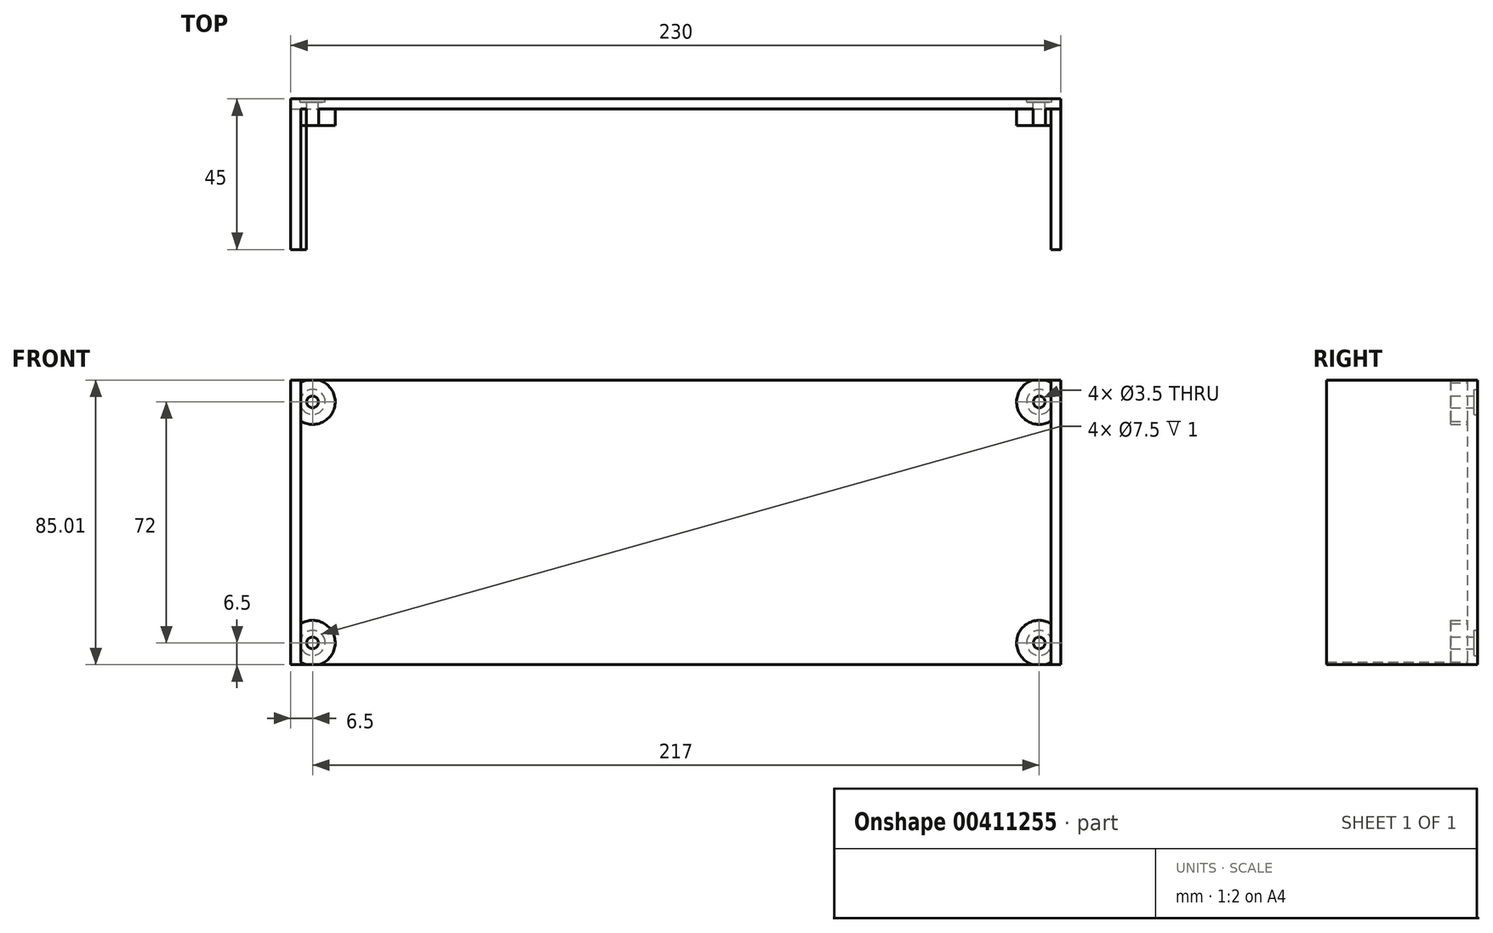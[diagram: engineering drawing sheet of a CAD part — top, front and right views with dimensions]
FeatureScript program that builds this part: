
annotation { "Feature Type Name" : "Feature", "Feature Type Description" : "" }
export const myFeature = defineFeature(function(context is Context, id is Id, definition is map)
    precondition{}
    {
        {
            var Q0;
            Q0=qCreatedBy(makeId("Front.planeOp"),FACE);
            var sketch = newSketch(context, id + "F0", { "sketchPlane" : qUnion([Q0])});
            skLineSegment(sketch, "E0.bottom", {"start": v(-115, 42.5) * mm, "end": v(115, 42.5) * mm});
            skLineSegment(sketch, "E0.top", {"start": v(-115, -42.5) * mm, "end": v(115, -42.5) * mm});
            skLineSegment(sketch, "E0.left", {"start": v(-115, 42.5) * mm, "end": v(-115, -42.5) * mm});
            skLineSegment(sketch, "E0.right", {"start": v(115, 42.5) * mm, "end": v(115, -42.5) * mm});
            skCircle(sketch, "E1", {"center": v(-108.5, 36) * mm, "radius": 1.75 * mm});
            skCircle(sketch, "E2", {"center": v(108.5, 36) * mm, "radius": 1.75 * mm});
            skCircle(sketch, "E3", {"center": v(108.5, -36) * mm, "radius": 1.75 * mm});
            skCircle(sketch, "E4", {"center": v(-108.5, -36) * mm, "radius": 1.75 * mm});
            skSolve(sketch);
        }
        {
            var Q0;
            Q0=makeQuery(id+"F0.imprint","IMPRINT",FACE,{"disambiguationData":[TD([[makeQuery(id+"F0.imprint","IMPRINT",EDGE,{"derivedFrom":sQuery(id+"F0.wireOp",EDGE,"E0.bottom")}),-1.0]])]});
            extrude(context, id + "F1", {"entities" : qUnion([Q0]), "depth" : 3 * mm});
        }
        {
            var Q0;
            Q0=qCreatedBy(makeId("Front.planeOp"),FACE);
            var sketch = newSketch(context, id + "F2", { "sketchPlane" : qUnion([Q0])});
            skCircle(sketch, "E5.0", {"center": v(108.5, 36) * mm, "radius": 3.75 * mm});
            skCircle(sketch, "E6.0", {"center": v(-108.5, 36) * mm, "radius": 3.75 * mm});
            skCircle(sketch, "E7.0", {"center": v(-108.5, -36) * mm, "radius": 3.75 * mm});
            skCircle(sketch, "E8.0", {"center": v(108.5, -36) * mm, "radius": 3.75 * mm});
            skSolve(sketch);
        }
        {
            var Q0;
            Q0 = qSketchRegion(id + "F2", true);
            extrude(context, id + "F3", {"entities" : qUnion([Q0]), "operationType" : NewBodyOperationType.REMOVE, "depth" : 1 * mm});
        }
        {
            var Q0;
            Q0=makeQuery(id+"F1.opExtrude","CAP_FACE",FACE,{"disambiguationData":[OSD([sQuery(id+"F0.wireOp",EDGE,"E0.bottom"),sQuery(id+"F0.wireOp",EDGE,"E0.top"),sQuery(id+"F0.wireOp",EDGE,"E0.left"),sQuery(id+"F0.wireOp",EDGE,"E0.right"),sQuery(id+"F0.wireOp",EDGE,"E1"),sQuery(id+"F0.wireOp",EDGE,"E2"),sQuery(id+"F0.wireOp",EDGE,"E3"),sQuery(id+"F0.wireOp",EDGE,"E4")])],"isStart":false});
            var sketch = newSketch(context, id + "F4", { "sketchPlane" : qUnion([Q0])});
            skCircle(sketch, "E9.0", {"center": v(-108.5, 36) * mm, "radius": 6.75 * mm});
            skCircle(sketch, "E10.0", {"center": v(-108.5, -36) * mm, "radius": 6.75 * mm});
            skCircle(sketch, "E11.0", {"center": v(108.5, 36) * mm, "radius": 6.75 * mm});
            skCircle(sketch, "E12.0", {"center": v(108.5, -36) * mm, "radius": 6.75 * mm});
            skSolve(sketch);
        }
        {
            var Q0;
            Q0=makeQuery(id+"F4.imprint","IMPRINT",FACE,{"disambiguationData":[TD([[makeQuery(id+"F4.imprint","IMPRINT",EDGE,{"derivedFrom":makeQuery(id+"F1.opExtrude","CAP_EDGE",EDGE,{"disambiguationData":[OSD([sQuery(id+"F0.wireOp",EDGE,"E1")])],"isStart":false})}),-1.0]])]});
            var Q1;
            Q1=makeQuery(id+"F4.imprint","IMPRINT",FACE,{"disambiguationData":[TD([[makeQuery(id+"F4.imprint","IMPRINT",EDGE,{"derivedFrom":makeQuery(id+"F1.opExtrude","CAP_EDGE",EDGE,{"disambiguationData":[OSD([sQuery(id+"F0.wireOp",EDGE,"E4")])],"isStart":false})}),-1.0]])]});
            var Q2;
            Q2=makeQuery(id+"F4.imprint","IMPRINT",FACE,{"disambiguationData":[TD([[makeQuery(id+"F4.imprint","IMPRINT",EDGE,{"derivedFrom":makeQuery(id+"F1.opExtrude","CAP_EDGE",EDGE,{"disambiguationData":[OSD([sQuery(id+"F0.wireOp",EDGE,"E2")])],"isStart":false})}),-1.0]])]});
            var Q3;
            Q3=makeQuery(id+"F4.imprint","IMPRINT",FACE,{"disambiguationData":[TD([[makeQuery(id+"F4.imprint","IMPRINT",EDGE,{"derivedFrom":makeQuery(id+"F1.opExtrude","CAP_EDGE",EDGE,{"disambiguationData":[OSD([sQuery(id+"F0.wireOp",EDGE,"E3")])],"isStart":false})}),-1.0]])]});
            extrude(context, id + "F5", {"entities" : qUnion([Q0, Q1, Q2, Q3]), "operationType" : NewBodyOperationType.ADD, "depth" : 5 * mm});
        }
        {
            var Q0;
            Q0=makeQuery(id+"F0.imprint","IMPRINT",FACE,{"disambiguationData":[TD([[makeQuery(id+"F0.imprint","IMPRINT",EDGE,{"derivedFrom":sQuery(id+"F0.wireOp",EDGE,"E4")}),1.0]])]});
            var Q1;
            Q1=makeQuery(id+"F0.imprint","IMPRINT",FACE,{"disambiguationData":[TD([[makeQuery(id+"F0.imprint","IMPRINT",EDGE,{"derivedFrom":sQuery(id+"F0.wireOp",EDGE,"E3")}),1.0]])]});
            var Q2;
            Q2=makeQuery(id+"F0.imprint","IMPRINT",FACE,{"disambiguationData":[TD([[makeQuery(id+"F0.imprint","IMPRINT",EDGE,{"derivedFrom":sQuery(id+"F0.wireOp",EDGE,"E2")}),1.0]])]});
            var Q3;
            Q3=makeQuery(id+"F0.imprint","IMPRINT",FACE,{"disambiguationData":[TD([[makeQuery(id+"F0.imprint","IMPRINT",EDGE,{"derivedFrom":sQuery(id+"F0.wireOp",EDGE,"E1")}),1.0]])]});
            var Q4;
            Q4=sQuery(id+"F0.wireOp",EDGE,"E2");
            var Q5;
            Q5=sQuery(id+"F0.wireOp",EDGE,"E3");
            var Q6;
            Q6=sQuery(id+"F0.wireOp",EDGE,"E1");
            var Q7;
            Q7=sQuery(id+"F0.wireOp",EDGE,"E4");
            extrude(context, id + "F6", {"entities" : qUnion([Q0, Q1, Q2, Q3]), "operationType" : NewBodyOperationType.REMOVE, "surfaceEntities" : qUnion([Q4, Q5, Q6, Q7]), "depth" : 8 * mm});
        }
        {
            var Q0;
            Q0=makeQuery(id+"F1.opExtrude","CAP_FACE",FACE,{"disambiguationData":[OSD([sQuery(id+"F0.wireOp",EDGE,"E0.bottom"),sQuery(id+"F0.wireOp",EDGE,"E0.top"),sQuery(id+"F0.wireOp",EDGE,"E0.left"),sQuery(id+"F0.wireOp",EDGE,"E0.right"),sQuery(id+"F0.wireOp",EDGE,"E1"),sQuery(id+"F0.wireOp",EDGE,"E2"),sQuery(id+"F0.wireOp",EDGE,"E3"),sQuery(id+"F0.wireOp",EDGE,"E4")])],"isStart":false});
            var sketch = newSketch(context, id + "F7", { "sketchPlane" : qUnion([Q0])});
            skLineSegment(sketch, "E13.0", {"start": v(-112, 42.5) * mm, "end": v(-112, -42.5) * mm});
            skLineSegment(sketch, "E14.0", {"start": v(112, 42.5) * mm, "end": v(112, -42.5) * mm});
            skLineSegment(sketch, "E15", {"start": v(-112, 42.5) * mm, "end": v(-115, 42.5) * mm});
            skLineSegment(sketch, "E16", {"start": v(-115, 42.5) * mm, "end": v(-115, -42.5) * mm});
            skLineSegment(sketch, "E17", {"start": v(-115, -42.5) * mm, "end": v(-112, -42.5) * mm});
            skLineSegment(sketch, "E18", {"start": v(112, -42.5) * mm, "end": v(115, -42.5) * mm});
            skLineSegment(sketch, "E19", {"start": v(115, -42.5) * mm, "end": v(115, 42.5) * mm});
            skLineSegment(sketch, "E20", {"start": v(115, 42.5) * mm, "end": v(112, 42.5) * mm});
            skSolve(sketch);
        }
        {
            var Q0;
            Q0 = qSketchRegion(id + "F7", true);
            var Q1;
            {var subQ0=sQuery(id+"F7.wireOp",EDGE,"E13.0");var subQ2=sQuery(id+"F4.wireOp",EDGE,"E9.0");var subQ3=sQuery(id+"F0.wireOp",EDGE,"E0.bottom");var subQ4=makeQuery(id+"F1.opExtrude","CAP_EDGE",EDGE,{"disambiguationData":[OSD([subQ3])],"isStart":false});var subQ5=makeQuery(id+"F4.imprint","INTERSECT",VERTEX,{"disambiguationData":[OD(0.0)],"derivedFrom":[subQ4,subQ2]});var subQ8=makeQuery(id+"F4.imprint","IMPRINT",EDGE,{"disambiguationData":[TD([[subQ5,-1.0]])],"derivedFrom":subQ2});var subQ13=makeQuery(id+"F5.opExtrude","CAP_EDGE",EDGE,{"disambiguationData":[OSD([subQ2]),TDD([subQ8])],"isStart":true});var subQ14=makeQuery(id+"F7.imprint","INTERSECT",VERTEX,{"derivedFrom":[subQ13,subQ0]});Q1=makeQuery(id+"F7.imprint","IMPRINT",FACE,{"disambiguationData":[TD([[makeQuery(id+"F7.imprint","IMPRINT",EDGE,{"disambiguationData":[TD([[subQ14,1.0]])],"derivedFrom":subQ0}),1.0]])]});}
            var Q2;
            {var subQ0=sQuery(id+"F7.wireOp",EDGE,"E13.0");var subQ1=sQuery(id+"F4.wireOp",EDGE,"E10.0");var subQ2=sQuery(id+"F0.wireOp",EDGE,"E0.left");var subQ3=makeQuery(id+"F1.opExtrude","CAP_EDGE",EDGE,{"disambiguationData":[OSD([subQ2])],"isStart":false});var subQ4=makeQuery(id+"F4.imprint","INTERSECT",VERTEX,{"disambiguationData":[OD(0.0)],"derivedFrom":[subQ3,subQ1]});var subQ8=makeQuery(id+"F4.imprint","IMPRINT",EDGE,{"disambiguationData":[TD([[subQ4,-1.0]])],"derivedFrom":subQ1});var subQ13=makeQuery(id+"F5.opExtrude","CAP_EDGE",EDGE,{"disambiguationData":[OSD([subQ1]),TDD([subQ8])],"isStart":true});var subQ14=makeQuery(id+"F7.imprint","INTERSECT",VERTEX,{"derivedFrom":[subQ13,subQ0]});Q2=makeQuery(id+"F7.imprint","IMPRINT",FACE,{"disambiguationData":[TD([[makeQuery(id+"F7.imprint","IMPRINT",EDGE,{"disambiguationData":[TD([[subQ14,-1.0]])],"derivedFrom":subQ0}),1.0]])]});}
            var Q3;
            {var subQ0=sQuery(id+"F7.wireOp",EDGE,"E14.0");var subQ2=sQuery(id+"F0.wireOp",EDGE,"E0.bottom");var subQ3=sQuery(id+"F4.wireOp",EDGE,"E11.0");var subQ4=makeQuery(id+"F1.opExtrude","CAP_EDGE",EDGE,{"disambiguationData":[OSD([subQ2])],"isStart":false});var subQ5=makeQuery(id+"F4.imprint","INTERSECT",VERTEX,{"disambiguationData":[OD(0.0)],"derivedFrom":[subQ4,subQ3]});var subQ8=makeQuery(id+"F4.imprint","IMPRINT",EDGE,{"disambiguationData":[TD([[subQ5,1.0]])],"derivedFrom":subQ3});var subQ13=makeQuery(id+"F5.opExtrude","CAP_EDGE",EDGE,{"disambiguationData":[OSD([subQ3]),TDD([subQ8])],"isStart":true});var subQ14=makeQuery(id+"F7.imprint","INTERSECT",VERTEX,{"derivedFrom":[subQ13,subQ0]});Q3=makeQuery(id+"F7.imprint","IMPRINT",FACE,{"disambiguationData":[TD([[makeQuery(id+"F7.imprint","IMPRINT",EDGE,{"disambiguationData":[TD([[subQ14,1.0]])],"derivedFrom":subQ0}),-1.0]])]});}
            var Q4;
            {var subQ0=sQuery(id+"F7.wireOp",EDGE,"E14.0");var subQ2=sQuery(id+"F0.wireOp",EDGE,"E0.top");var subQ3=sQuery(id+"F4.wireOp",EDGE,"E12.0");var subQ4=makeQuery(id+"F1.opExtrude","CAP_EDGE",EDGE,{"disambiguationData":[OSD([subQ2])],"isStart":false});var subQ5=makeQuery(id+"F4.imprint","INTERSECT",VERTEX,{"disambiguationData":[OD(1.0)],"derivedFrom":[subQ4,subQ3]});var subQ8=makeQuery(id+"F4.imprint","IMPRINT",EDGE,{"disambiguationData":[TD([[subQ5,-1.0]])],"derivedFrom":subQ3});var subQ13=makeQuery(id+"F5.opExtrude","CAP_EDGE",EDGE,{"disambiguationData":[OSD([subQ3]),TDD([subQ8])],"isStart":true});var subQ14=makeQuery(id+"F7.imprint","INTERSECT",VERTEX,{"derivedFrom":[subQ13,subQ0]});Q4=makeQuery(id+"F7.imprint","IMPRINT",FACE,{"disambiguationData":[TD([[makeQuery(id+"F7.imprint","IMPRINT",EDGE,{"disambiguationData":[TD([[subQ14,-1.0]])],"derivedFrom":subQ0}),-1.0]])]});}
            extrude(context, id + "F8", {"entities" : qUnion([Q0, Q1, Q2, Q3, Q4]), "operationType" : NewBodyOperationType.ADD, "depth" : 42 * mm});
        }
    });
